# Revit family: Outlet-Bath-Irwell Pin Lever-Wall
name_source: partatom
category: Plumbing Fixtures
revit_build: Autodesk Revit 2013 (Build: 20121003_2115(x64)
units: mm (PartAtom-declared; Revit-internal decimal feet)

## types (2) — shared parameters
Assembly Code = C1030210
CW Connection = Yes
CWFU = 3
Connector Radius = 10 mm  [stored 0.0328084 ft]
Default Elevation = 500 mm  [stored 1.64042 ft]
HW Connection = Yes
HWFU = 3
Manufacturer = GWA Bathrooms & Kitchens
Material_ANZRS = Metal-Chrome-Caroma
URL = http://www.irwell.com.au
Vent Connection = No
Waste Connection = No
zero-valued in all types: Cost

## per-type parameters (varying)
| type | Large | Length_ANZRS | Model | Type Comments |
| 150mm | No | 170 mm | 872573C | Irwell Pin Lever Bath Outlet - 150mm |
| 215mm | Yes | 235 mm | 872574C | Irwell Pin Lever Bath Outlet - 215mm |

note: [stored X ft] marks values corroborated as IEEE doubles in the binary element streams (Revit-internal decimal feet)

## geometry (parser evidence)
native form markers: Blend x14, Sweep x1
no freeform markers — native parametric forms only
